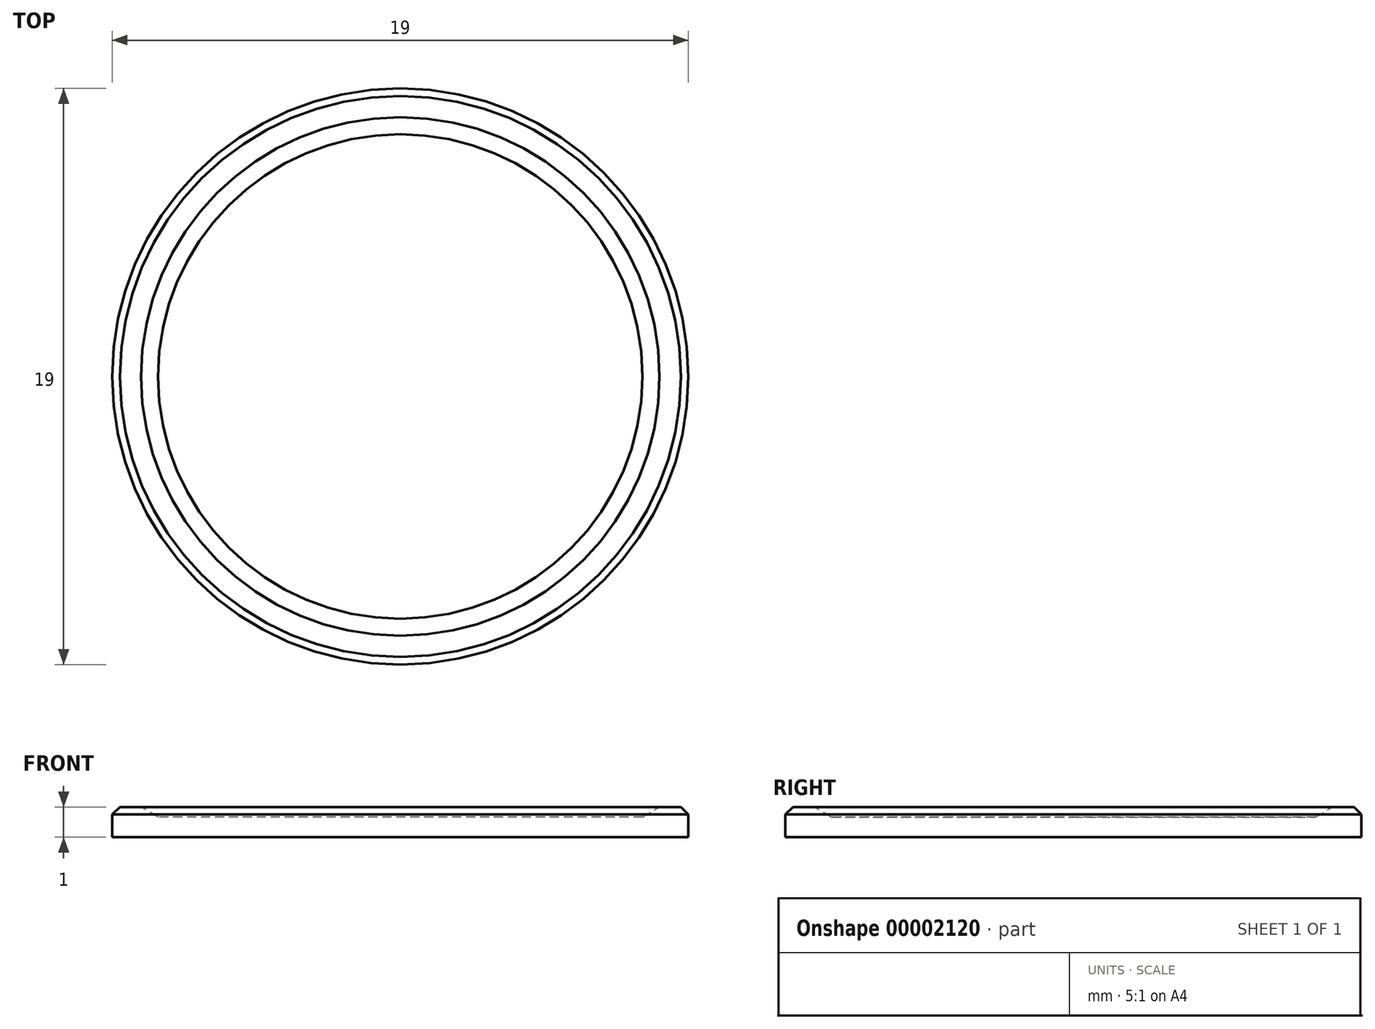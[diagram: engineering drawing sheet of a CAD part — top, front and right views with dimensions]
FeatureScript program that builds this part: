
annotation { "Feature Type Name" : "Feature", "Feature Type Description" : "" }
export const myFeature = defineFeature(function(context is Context, id is Id, definition is map)
    precondition{}
    {
        {
            var Q0;
            Q0=qCreatedBy(makeId("Top.planeOp"),FACE);
            var sketch = newSketch(context, id + "F0", { "sketchPlane" : qUnion([Q0])});
            skCircle(sketch, "E0", {"center": v(0, 0) * mm, "radius": 9.5 * mm});
            skSolve(sketch);
        }
        {
            var Q0;
            Q0=makeQuery(id+"F0.imprint","IMPRINT",FACE,{"disambiguationData":[TD([[makeQuery(id+"F0.imprint","IMPRINT",EDGE,{"derivedFrom":sQuery(id+"F0.wireOp",EDGE,"E0")}),1.0]])]});
            extrude(context, id + "F1", {"entities" : qUnion([Q0]), "depth" : 1 * mm});
        }
        {
            var Q0;
            Q0=qCreatedBy(makeId("Front.planeOp"),FACE);
            var sketch = newSketch(context, id + "F2", { "sketchPlane" : qUnion([Q0])});
            skLineSegment(sketch, "E1", {"start": v(0, 1.27) * mm, "end": v(0, 0.67) * mm});
            skLineSegment(sketch, "E2", {"start": v(0, 0.67) * mm, "end": v(7.99, 0.67) * mm});
            skLineSegment(sketch, "E3", {"start": v(7.99, 0.67) * mm, "end": v(9, 1.27) * mm});
            skLineSegment(sketch, "E4", {"start": v(9, 1.27) * mm, "end": v(0, 1.27) * mm});
            skLineSegment(sketch, "E5", {"start": v(0, 1.7) * mm, "end": v(0, 3.3) * mm, "construction": true});
            skSolve(sketch);
        }
        {
            var Q0;
            Q0 = qSketchRegion(id + "F2", true);
            var Q1;
            Q1=sQuery(id+"F2.wireOp",EDGE,"E5");
            revolve(context, id + "F3", {"operationType" : NewBodyOperationType.REMOVE, "entities" : qUnion([Q0]), "axis" : qUnion([Q1]), "revolveType" : RevolveType.FULL, "oppositeDirection" : true});
        }
        {
            var Q0;
            Q0=makeQuery(id+"F1.opExtrude","CAP_EDGE",EDGE,{"disambiguationData":[OSD([sQuery(id+"F0.wireOp",EDGE,"E0")])],"isStart":false});
            chamfer(context, id + "F4", {"entities" : qUnion([Q0]), "width" : .25 * mm, "tangentPropagation" : true});
        }
    });
